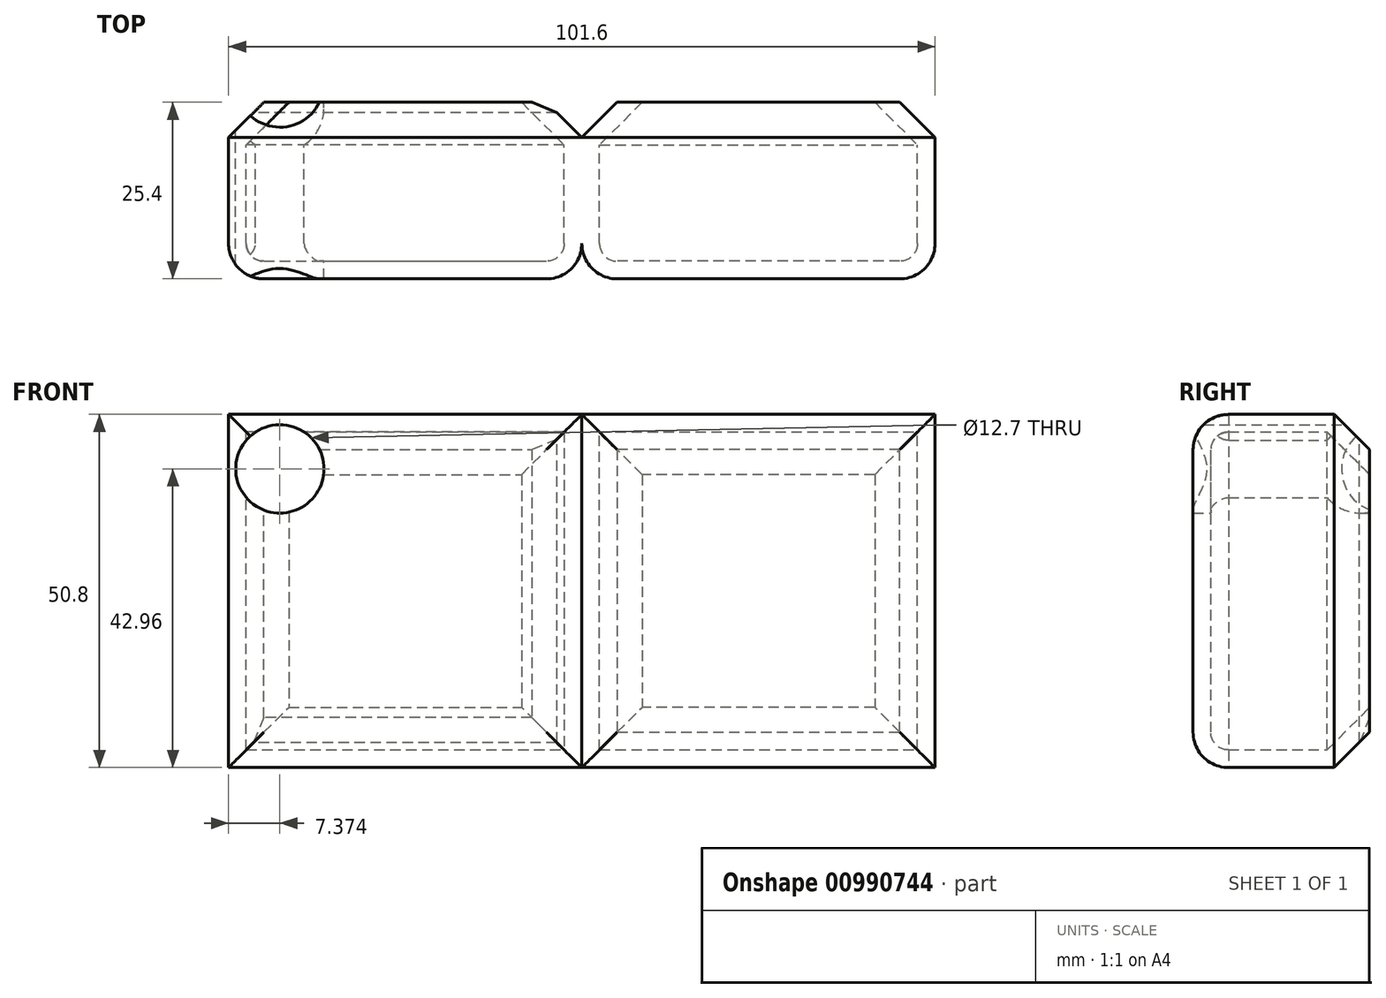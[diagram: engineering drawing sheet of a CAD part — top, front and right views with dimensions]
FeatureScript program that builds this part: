
annotation { "Feature Type Name" : "Feature", "Feature Type Description" : "" }
export const myFeature = defineFeature(function(context is Context, id is Id, definition is map)
    precondition{}
    {
        {
            var Q0;
            Q0=qCreatedBy(makeId("Front.planeOp"),FACE);
            var sketch = newSketch(context, id + "F0", { "sketchPlane" : qUnion([Q0])});
            skLineSegment(sketch, "E0.bottom", {"start": v(-25.4, 25.4) * mm, "end": v(25.4, 25.4) * mm});
            skLineSegment(sketch, "E0.top", {"start": v(-25.4, -25.4) * mm, "end": v(25.4, -25.4) * mm});
            skLineSegment(sketch, "E0.left", {"start": v(-25.4, 25.4) * mm, "end": v(-25.4, -25.4) * mm});
            skLineSegment(sketch, "E0.right", {"start": v(25.4, 25.4) * mm, "end": v(25.4, -25.4) * mm});
            skPoint(sketch, "E0.middle", {"position": v(0, 0) * mm});
            skSolve(sketch);
        }
        {
            var Q0;
            Q0=makeQuery(id+"F0.imprint","IMPRINT",FACE,{"disambiguationData":[TD([[makeQuery(id+"F0.imprint","IMPRINT",EDGE,{"derivedFrom":sQuery(id+"F0.wireOp",EDGE,"E0.bottom")}),-1.0]])]});
            extrude(context, id + "F1", {"entities" : qUnion([Q0]), "depth" : 25.4 * mm, "offsetDistance" : 25.4 * mm});
        }
        {
            var Q0;
            Q0=qCreatedBy(makeId("Front.planeOp"),FACE);
            var sketch = newSketch(context, id + "F2", { "sketchPlane" : qUnion([Q0])});
            skCircle(sketch, "E1", {"center": v(-18.03, 17.56) * mm, "radius": 6.73 * mm});
            skSolve(sketch);
        }
        {
            var Q0;
            Q0=makeQuery(id+"F1.opExtrude","CAP_FACE",FACE,{"disambiguationData":[OSD([sQuery(id+"F0.wireOp",EDGE,"E0.bottom"),sQuery(id+"F0.wireOp",EDGE,"E0.top"),sQuery(id+"F0.wireOp",EDGE,"E0.left"),sQuery(id+"F0.wireOp",EDGE,"E0.right")])],"isStart":false});
            var Q1;
            Q1=makeQuery(id+"F1.opExtrude","CAP_EDGE",EDGE,{"disambiguationData":[OSD([sQuery(id+"F0.wireOp",EDGE,"E0.bottom")])],"isStart":false});
            fillet(context, id + "F3", {"entities" : qUnion([Q0, Q1]), "radius" : 5.08 * mm, "tangentPropagation" : true, "allowEdgeOverflow" : false});
        }
        {
            var Q0;
            Q0=makeQuery(id+"F1.opExtrude","CAP_FACE",FACE,{"disambiguationData":[OSD([sQuery(id+"F0.wireOp",EDGE,"E0.bottom"),sQuery(id+"F0.wireOp",EDGE,"E0.top"),sQuery(id+"F0.wireOp",EDGE,"E0.left"),sQuery(id+"F0.wireOp",EDGE,"E0.right")])],"isStart":true});
            chamfer(context, id + "F4", {"entities" : qUnion([Q0]), "width" : 5.08 * mm, "tangentPropagation" : true});
        }
        {
            var Q0;
            Q0=makeQuery(id+"F1.opExtrude","CAP_FACE",FACE,{"disambiguationData":[OSD([sQuery(id+"F0.wireOp",EDGE,"E0.bottom"),sQuery(id+"F0.wireOp",EDGE,"E0.top"),sQuery(id+"F0.wireOp",EDGE,"E0.left"),sQuery(id+"F0.wireOp",EDGE,"E0.right")])],"isStart":true});
            shell(context, id + "F5", {"entities" : qUnion([Q0]), "thickness" : 2.54 * mm});
        }
        {
            var Q0;
            Q0=makeQuery(id+"F1.opExtrude","SWEPT_BODY",BODY,{"disambiguationData":[OSD([sQuery(id+"F0.wireOp",EDGE,"E0.bottom"),sQuery(id+"F0.wireOp",EDGE,"E0.top"),sQuery(id+"F0.wireOp",EDGE,"E0.left"),sQuery(id+"F0.wireOp",EDGE,"E0.right")])]});
            var Q1;
            Q1=makeQuery(id+"F1.opExtrude","SWEPT_FACE",FACE,{"disambiguationData":[OSD([sQuery(id+"F0.wireOp",EDGE,"E0.right")])]});
            mirror(context, id + "F6", {"operationType" : NewBodyOperationType.ADD, "entities" : qUnion([Q0]), "mirrorPlane" : qUnion([Q1])});
        }
        {
            var Q0;
            Q0=sQuery(id+"F2.wireOp",VERTEX,"E1.center");
            var Q1;
            Q1=makeQuery(id+"F1.opExtrude","SWEPT_BODY",BODY,{"disambiguationData":[OSD([sQuery(id+"F0.wireOp",EDGE,"E0.bottom"),sQuery(id+"F0.wireOp",EDGE,"E0.top"),sQuery(id+"F0.wireOp",EDGE,"E0.left"),sQuery(id+"F0.wireOp",EDGE,"E0.right")])]});
            hole(context, id + "F7", {"style" : HoleStyle.SIMPLE, "endStyle" : HoleEndStyle.THROUGH, "oppositeDirection" : true, "holeDiameter" : 12.7 * mm, "majorDiameter" : 6.35 * mm, "isTappedThrough" : true, "tappedDepth" : 12.7 * mm, "tapClearance" : 3, "locations" : qUnion([Q0]), "scope" : qUnion([Q1])});
        }
        {
            var Q0;
            {var subQ0=sQuery(id+"F0.wireOp",EDGE,"E0.top");Q0=makeQuery(id+"F4.opChamfer","BLEND_EDGE",EDGE,{"blendedFrom":[makeQuery(id+"F1.opExtrude","CAP_EDGE",EDGE,{"disambiguationData":[OSD([subQ0])],"isStart":true}),makeQuery(id+"F1.opExtrude","CAP_FACE",FACE,{"disambiguationData":[OSD([sQuery(id+"F0.wireOp",EDGE,"E0.bottom"),subQ0,sQuery(id+"F0.wireOp",EDGE,"E0.left"),sQuery(id+"F0.wireOp",EDGE,"E0.right")])],"isStart":true})],"blendedInto":[makeQuery(id+"F1.opExtrude","CAP_FACE",FACE,{"disambiguationData":[OSD([sQuery(id+"F0.wireOp",EDGE,"E0.bottom"),subQ0,sQuery(id+"F0.wireOp",EDGE,"E0.left"),sQuery(id+"F0.wireOp",EDGE,"E0.right")])],"isStart":true})]});}
            var Q1;
            {var subQ0=sQuery(id+"F0.wireOp",EDGE,"E0.right");Q1=makeQuery(id+"F4.opChamfer","BLEND_EDGE",EDGE,{"blendedFrom":[makeQuery(id+"F1.opExtrude","CAP_EDGE",EDGE,{"disambiguationData":[OSD([subQ0])],"isStart":true}),makeQuery(id+"F1.opExtrude","CAP_FACE",FACE,{"disambiguationData":[OSD([sQuery(id+"F0.wireOp",EDGE,"E0.bottom"),sQuery(id+"F0.wireOp",EDGE,"E0.top"),sQuery(id+"F0.wireOp",EDGE,"E0.left"),subQ0])],"isStart":true})],"blendedInto":[makeQuery(id+"F1.opExtrude","CAP_FACE",FACE,{"disambiguationData":[OSD([sQuery(id+"F0.wireOp",EDGE,"E0.bottom"),sQuery(id+"F0.wireOp",EDGE,"E0.top"),sQuery(id+"F0.wireOp",EDGE,"E0.left"),subQ0])],"isStart":true})]});}
            chamfer(context, id + "F8", {"entities" : qUnion([Q0, Q1]), "width" : 5.08 * mm, "tangentPropagation" : true});
        }
    });
